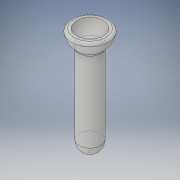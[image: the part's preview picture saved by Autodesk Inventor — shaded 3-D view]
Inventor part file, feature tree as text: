
AUTODESK INVENTOR PART (.ipt)
format: ipt  version: 2018 (Build 220112000, 112)  size: 144,384 bytes
history: native  units: mm
features: revolve x1, sketch x1
ambient origin geometry x8: Origin, YZ Plane, XZ Plane, XY Plane, X Axis, Y Axis, Z Axis, Center Point
bodies: Solid1 (feature_tree)
feature tree (2):
  revolve  "Revolution1"  [1 undecoded]
  sketch  "Sketch1"  dims[d0=20.0mm d1=5.0mm d2=7.0mm d3=2.0mm d4=2.0mm d5=0.25mm d6=0.25mm d7=1.0mm d8=1.0mm d9=90.0deg]
note: 1 required parameter value undecoded (feature->parameter linkage not recoverable at this tier; creation-order binding heuristic only, values carry confidence <= 0.55)
